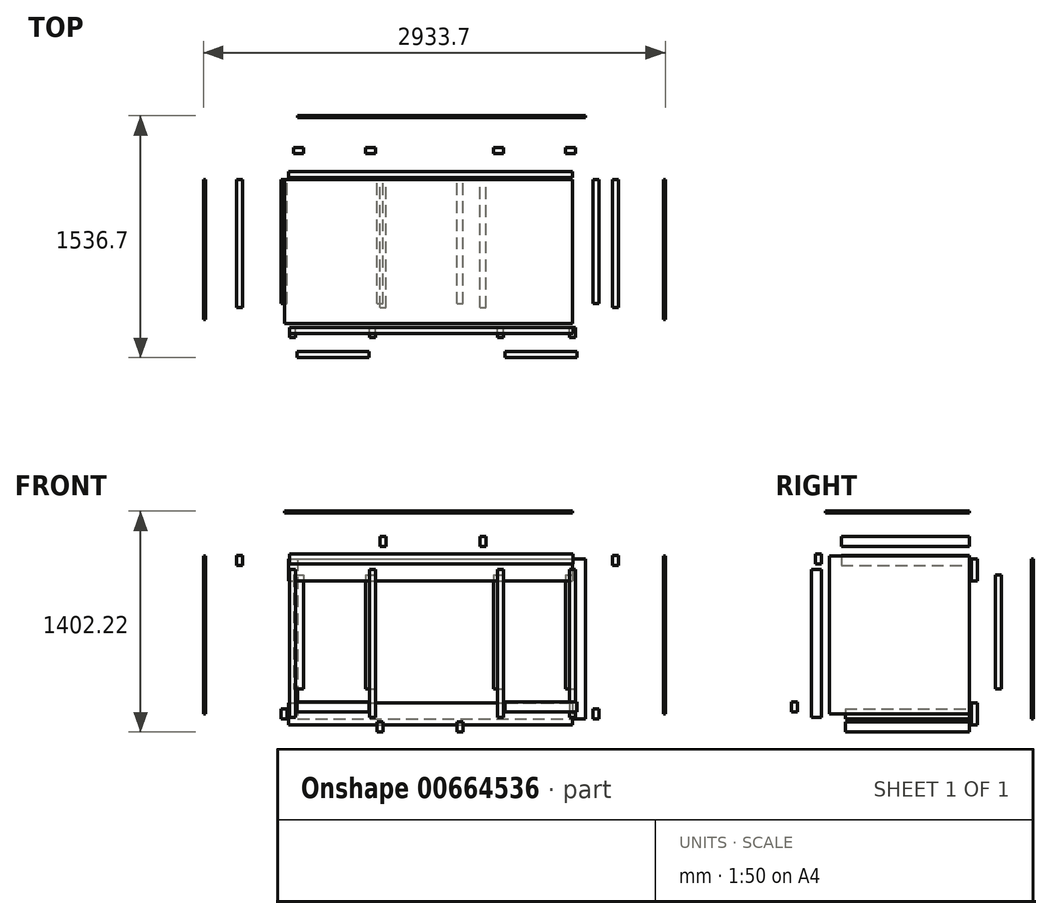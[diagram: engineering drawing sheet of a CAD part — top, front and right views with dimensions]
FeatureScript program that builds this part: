
annotation { "Feature Type Name" : "Feature", "Feature Type Description" : "" }
export const myFeature = defineFeature(function(context is Context, id is Id, definition is map)
    precondition{}
    {
        {
            var Q0;
            Q0=qCreatedBy(makeId("Front.planeOp"),FACE);
            var sketch = newSketch(context, id + "F0", { "sketchPlane" : qUnion([Q0])});
            skLineSegment(sketch, "E0.bottom", {"start": v(-77.6, 167.5) * mm, "end": v(1751.2, 167.5) * mm});
            skLineSegment(sketch, "E0.top", {"start": v(-77.6, 154.8) * mm, "end": v(1751.2, 154.8) * mm});
            skLineSegment(sketch, "E0.left", {"start": v(-77.6, 167.5) * mm, "end": v(-77.6, 154.8) * mm});
            skLineSegment(sketch, "E0.right", {"start": v(1751.2, 167.5) * mm, "end": v(1751.2, 154.8) * mm});
            skSolve(sketch);
        }
        {
            var Q0;
            Q0=qSketchRegion(id+"F0",true);
            extrude(context, id + "F1", {"entities" : qUnion([Q0]), "depth" : 914.4 * mm, "offsetDistance" : 25.4 * mm});
        }
        {
            var Q0;
            Q0=qCreatedBy(makeId("Front.planeOp"),FACE);
            var sketch = newSketch(context, id + "F2", { "sketchPlane" : qUnion([Q0])});
            skLineSegment(sketch, "E1.bottom", {"start": v(-96.67, 148.12) * mm, "end": v(1706.73, 148.12) * mm});
            skLineSegment(sketch, "E1.top", {"start": v(-96.67, 84.62) * mm, "end": v(1706.73, 84.62) * mm});
            skLineSegment(sketch, "E1.left", {"start": v(-96.67, 148.12) * mm, "end": v(-96.67, 84.62) * mm});
            skLineSegment(sketch, "E1.right", {"start": v(1706.73, 148.12) * mm, "end": v(1706.73, 84.62) * mm});
            skSolve(sketch);
        }
        {
            var Q0;
            Q0=qSketchRegion(id+"F2",true);
            extrude(context, id + "F3", {"entities" : qUnion([Q0]), "depth" : 38.1 * mm, "offsetDistance" : 25.4 * mm});
        }
        {
            var Q0;
            Q0=makeQuery(id+"F3.opExtrude","SWEPT_BODY",BODY,{"disambiguationData":[OSD([sQuery(id+"F2.wireOp",EDGE,"E1.bottom"),sQuery(id+"F2.wireOp",EDGE,"E1.top"),sQuery(id+"F2.wireOp",EDGE,"E1.left"),sQuery(id+"F2.wireOp",EDGE,"E1.right")])]});
            transform(context, id + "F4", {"entities" : qUnion([Q0]), "transformType" : TransformType.TRANSLATION_3D, "dx" : -762 * mm, "dy" : -939.8 * mm, "dz" : 0 * mm, "makeCopy" : false});
        }
        {
            var Q0;
            Q0=makeQuery(id+"F1.opExtrude","SWEPT_BODY",BODY,{"disambiguationData":[OSD([sQuery(id+"F0.wireOp",EDGE,"E0.bottom"),sQuery(id+"F0.wireOp",EDGE,"E0.top"),sQuery(id+"F0.wireOp",EDGE,"E0.left"),sQuery(id+"F0.wireOp",EDGE,"E0.right")])]});
            transform(context, id + "F5", {"entities" : qUnion([Q0]), "transformType" : TransformType.TRANSLATION_3D, "dx" : -812.8 * mm, "dy" : 0 * mm, "dz" : 0 * mm, "makeCopy" : false});
        }
        {
            var Q0;
            Q0=qCreatedBy(makeId("Front.planeOp"),FACE);
            var sketch = newSketch(context, id + "F6", { "sketchPlane" : qUnion([Q0])});
            skLineSegment(sketch, "E2.bottom", {"start": v(-857.8, 557.43) * mm, "end": v(-819.7, 557.43) * mm});
            skLineSegment(sketch, "E2.top", {"start": v(-857.8, -382.37) * mm, "end": v(-819.7, -382.37) * mm});
            skLineSegment(sketch, "E2.left", {"start": v(-857.8, 557.43) * mm, "end": v(-857.8, -382.37) * mm});
            skLineSegment(sketch, "E2.right", {"start": v(-819.7, 557.43) * mm, "end": v(-819.7, -382.37) * mm});
            skSolve(sketch);
        }
        {
            var Q0;
            Q0=qSketchRegion(id+"F6",true);
            extrude(context, id + "F7", {"entities" : qUnion([Q0]), "depth" : 63.5 * mm, "offsetDistance" : 25.4 * mm});
        }
        {
            var Q0;
            Q0=makeQuery(id+"F7.opExtrude","SWEPT_BODY",BODY,{"disambiguationData":[OSD([sQuery(id+"F6.wireOp",EDGE,"E2.bottom"),sQuery(id+"F6.wireOp",EDGE,"E2.top"),sQuery(id+"F6.wireOp",EDGE,"E2.left"),sQuery(id+"F6.wireOp",EDGE,"E2.right")])]});
            transform(context, id + "F8", {"entities" : qUnion([Q0]), "transformType" : TransformType.TRANSLATION_3D, "dx" : 0 * mm, "dy" : -939.8 * mm, "dz" : -508 * mm, "makeCopy" : false});
        }
        {
            var Q0;
            Q0=makeQuery(id+"F7.opExtrude","SWEPT_BODY",BODY,{"disambiguationData":[OSD([sQuery(id+"F6.wireOp",EDGE,"E2.bottom"),sQuery(id+"F6.wireOp",EDGE,"E2.top"),sQuery(id+"F6.wireOp",EDGE,"E2.left"),sQuery(id+"F6.wireOp",EDGE,"E2.right")])]});
            transform(context, id + "F9", {"entities" : qUnion([Q0]), "transformType" : TransformType.TRANSLATION_3D, "dx" : 1778 * mm, "dy" : 0 * mm, "dz" : 0 * mm, "makeCopy" : true});
        }
        {
            var Q0;
            Q0=makeQuery(id+"F7.opExtrude","SWEPT_BODY",BODY,{"disambiguationData":[OSD([sQuery(id+"F6.wireOp",EDGE,"E2.bottom"),sQuery(id+"F6.wireOp",EDGE,"E2.top"),sQuery(id+"F6.wireOp",EDGE,"E2.left"),sQuery(id+"F6.wireOp",EDGE,"E2.right")])]});
            transform(context, id + "F10", {"entities" : qUnion([Q0]), "transformType" : TransformType.TRANSLATION_3D, "dx" : 508 * mm, "dy" : 0 * mm, "dz" : 0 * mm, "makeCopy" : true});
        }
        {
            var Q0;
            Q0=makeQuery(id+"F7.opExtrude","SWEPT_BODY",BODY,{"disambiguationData":[OSD([sQuery(id+"F6.wireOp",EDGE,"E2.bottom"),sQuery(id+"F6.wireOp",EDGE,"E2.top"),sQuery(id+"F6.wireOp",EDGE,"E2.left"),sQuery(id+"F6.wireOp",EDGE,"E2.right")])]});
            transform(context, id + "F11", {"entities" : qUnion([Q0]), "transformType" : TransformType.TRANSLATION_3D, "dx" : 1320.8 * mm, "dy" : 0 * mm, "dz" : 0 * mm, "makeCopy" : true});
        }
        {
            var Q0;
            Q0=qCreatedBy(makeId("Front.planeOp"),FACE);
            var sketch = newSketch(context, id + "F12", { "sketchPlane" : qUnion([Q0])});
            skLineSegment(sketch, "E3.bottom", {"start": v(-940.02, 138.97) * mm, "end": v(-901.92, 138.97) * mm});
            skLineSegment(sketch, "E3.top", {"start": v(-940.02, 75.47) * mm, "end": v(-901.92, 75.47) * mm});
            skLineSegment(sketch, "E3.left", {"start": v(-940.02, 138.97) * mm, "end": v(-940.02, 75.47) * mm});
            skLineSegment(sketch, "E3.right", {"start": v(-901.92, 138.97) * mm, "end": v(-901.92, 75.47) * mm});
            skSolve(sketch);
        }
        {
            var Q0;
            Q0=qSketchRegion(id+"F12",true);
            extrude(context, id + "F13", {"entities" : qUnion([Q0]), "depth" : 812.8 * mm, "offsetDistance" : 25.4 * mm});
        }
        {
            var Q0;
            Q0=makeQuery(id+"F13.opExtrude","SWEPT_BODY",BODY,{"disambiguationData":[OSD([sQuery(id+"F12.wireOp",EDGE,"E3.bottom"),sQuery(id+"F12.wireOp",EDGE,"E3.top"),sQuery(id+"F12.wireOp",EDGE,"E3.left"),sQuery(id+"F12.wireOp",EDGE,"E3.right")])]});
            transform(context, id + "F14", {"entities" : qUnion([Q0]), "transformType" : TransformType.TRANSLATION_3D, "dx" : 1879.6 * mm, "dy" : 0 * mm, "dz" : 0 * mm, "makeCopy" : true});
        }
        {
            var Q0;
            Q0=qCreatedBy(makeId("Front.planeOp"),FACE);
            var sketch = newSketch(context, id + "F15", { "sketchPlane" : qUnion([Q0])});
            skLineSegment(sketch, "E4.bottom", {"start": v(-862.45, 42) * mm, "end": v(940.95, 42) * mm});
            skLineSegment(sketch, "E4.top", {"start": v(-862.45, -97.7) * mm, "end": v(940.95, -97.7) * mm});
            skLineSegment(sketch, "E4.left", {"start": v(-862.45, 42) * mm, "end": v(-862.45, -97.7) * mm});
            skLineSegment(sketch, "E4.right", {"start": v(940.95, 42) * mm, "end": v(940.95, -97.7) * mm});
            skSolve(sketch);
        }
        {
            var Q0;
            Q0=qSketchRegion(id+"F15",true);
            extrude(context, id + "F16", {"entities" : qUnion([Q0]), "depth" : 38.1 * mm, "offsetDistance" : 25.4 * mm});
        }
        {
            var Q0;
            Q0=makeQuery(id+"F16.opExtrude","SWEPT_BODY",BODY,{"disambiguationData":[OSD([sQuery(id+"F15.wireOp",EDGE,"E4.bottom"),sQuery(id+"F15.wireOp",EDGE,"E4.top"),sQuery(id+"F15.wireOp",EDGE,"E4.left"),sQuery(id+"F15.wireOp",EDGE,"E4.right")])]});
            transform(context, id + "F17", {"entities" : qUnion([Q0]), "transformType" : TransformType.TRANSLATION_3D, "dx" : 0 * mm, "dy" : 0 * mm, "dz" : -762 * mm, "makeCopy" : true});
        }
        {
            var Q0;
            Q0=makeQuery(id+"F13.opExtrude","SWEPT_BODY",BODY,{"disambiguationData":[OSD([sQuery(id+"F12.wireOp",EDGE,"E3.bottom"),sQuery(id+"F12.wireOp",EDGE,"E3.top"),sQuery(id+"F12.wireOp",EDGE,"E3.left"),sQuery(id+"F12.wireOp",EDGE,"E3.right")])]});
            transform(context, id + "F18", {"entities" : qUnion([Q0]), "transformType" : TransformType.TRANSLATION_3D, "dx" : 0 * mm, "dy" : 0 * mm, "dz" : -939.8 * mm, "makeCopy" : true});
        }
        {
            var Q0;
            Q0=makeQuery(id+"F14.opPattern","COPY",BODY,{"derivedFrom":makeQuery(id+"F13.opExtrude","SWEPT_BODY",BODY,{"disambiguationData":[OSD([sQuery(id+"F12.wireOp",EDGE,"E3.bottom"),sQuery(id+"F12.wireOp",EDGE,"E3.top"),sQuery(id+"F12.wireOp",EDGE,"E3.left"),sQuery(id+"F12.wireOp",EDGE,"E3.right")])]}),"instanceName":"1"});
            transform(context, id + "F19", {"entities" : qUnion([Q0]), "transformType" : TransformType.TRANSLATION_3D, "dx" : 0 * mm, "dy" : 0 * mm, "dz" : -939.8 * mm, "makeCopy" : true});
        }
        {
            var Q0;
            Q0=qCreatedBy(makeId("Front.planeOp"),FACE);
            var sketch = newSketch(context, id + "F20", { "sketchPlane" : qUnion([Q0])});
            skLineSegment(sketch, "E5.bottom", {"start": v(-809.8, -791.75) * mm, "end": v(-352.6, -791.75) * mm});
            skLineSegment(sketch, "E5.top", {"start": v(-809.8, -855.25) * mm, "end": v(-352.6, -855.25) * mm});
            skLineSegment(sketch, "E5.left", {"start": v(-809.8, -791.75) * mm, "end": v(-809.8, -855.25) * mm});
            skLineSegment(sketch, "E5.right", {"start": v(-352.6, -791.75) * mm, "end": v(-352.6, -855.25) * mm});
            skSolve(sketch);
        }
        {
            var Q0;
            Q0=qSketchRegion(id+"F20",true);
            extrude(context, id + "F21", {"entities" : qUnion([Q0]), "depth" : 38.1 * mm, "offsetDistance" : 25.4 * mm});
        }
        {
            var Q0;
            Q0=makeQuery(id+"F21.opExtrude","SWEPT_BODY",BODY,{"disambiguationData":[OSD([sQuery(id+"F20.wireOp",EDGE,"E5.bottom"),sQuery(id+"F20.wireOp",EDGE,"E5.top"),sQuery(id+"F20.wireOp",EDGE,"E5.left"),sQuery(id+"F20.wireOp",EDGE,"E5.right")])]});
            transform(context, id + "F22", {"entities" : qUnion([Q0]), "transformType" : TransformType.TRANSLATION_3D, "dx" : 0 * mm, "dy" : -965.2 * mm, "dz" : 0 * mm, "makeCopy" : false});
        }
        {
            var Q0;
            Q0=makeQuery(id+"F21.opExtrude","SWEPT_BODY",BODY,{"disambiguationData":[OSD([sQuery(id+"F20.wireOp",EDGE,"E5.bottom"),sQuery(id+"F20.wireOp",EDGE,"E5.top"),sQuery(id+"F20.wireOp",EDGE,"E5.left"),sQuery(id+"F20.wireOp",EDGE,"E5.right")])]});
            transform(context, id + "F23", {"entities" : qUnion([Q0]), "transformType" : TransformType.TRANSLATION_3D, "dx" : 1320.8 * mm, "dy" : 0 * mm, "dz" : 0 * mm, "makeCopy" : true});
        }
        {
            var Q0;
            Q0=makeQuery(id+"F13.opExtrude","SWEPT_BODY",BODY,{"disambiguationData":[OSD([sQuery(id+"F12.wireOp",EDGE,"E3.bottom"),sQuery(id+"F12.wireOp",EDGE,"E3.top"),sQuery(id+"F12.wireOp",EDGE,"E3.left"),sQuery(id+"F12.wireOp",EDGE,"E3.right")])]});
            transform(context, id + "F24", {"entities" : qUnion([Q0]), "transformType" : TransformType.TRANSLATION_3D, "dx" : 508 * mm, "dy" : 0 * mm, "dz" : 0 * mm, "makeCopy" : true});
        }
        {
            var Q0;
            Q0=makeQuery(id+"F13.opExtrude","SWEPT_BODY",BODY,{"disambiguationData":[OSD([sQuery(id+"F12.wireOp",EDGE,"E3.bottom"),sQuery(id+"F12.wireOp",EDGE,"E3.top"),sQuery(id+"F12.wireOp",EDGE,"E3.left"),sQuery(id+"F12.wireOp",EDGE,"E3.right")])]});
            transform(context, id + "F25", {"entities" : qUnion([Q0]), "transformType" : TransformType.TRANSLATION_3D, "dx" : 1320.8 * mm, "dy" : 0 * mm, "dz" : 0 * mm, "makeCopy" : true});
        }
        {
            var Q0;
            Q0=qCreatedBy(makeId("Front.planeOp"),FACE);
            var sketch = newSketch(context, id + "F26", { "sketchPlane" : qUnion([Q0])});
            skLineSegment(sketch, "E6.bottom", {"start": v(-831.16, 15.51) * mm, "end": v(-767.66, 15.51) * mm});
            skLineSegment(sketch, "E6.top", {"start": v(-831.16, -708.39) * mm, "end": v(-767.66, -708.39) * mm});
            skLineSegment(sketch, "E6.left", {"start": v(-831.16, 15.51) * mm, "end": v(-831.16, -708.39) * mm});
            skLineSegment(sketch, "E6.right", {"start": v(-767.66, 15.51) * mm, "end": v(-767.66, -708.39) * mm});
            skSolve(sketch);
        }
        {
            var Q0;
            Q0=qSketchRegion(id+"F26",true);
            extrude(context, id + "F27", {"entities" : qUnion([Q0]), "depth" : 38.1 * mm, "offsetDistance" : 25.4 * mm});
        }
        {
            var Q0;
            Q0=makeQuery(id+"F27.opExtrude","SWEPT_BODY",BODY,{"disambiguationData":[OSD([sQuery(id+"F26.wireOp",EDGE,"E6.bottom"),sQuery(id+"F26.wireOp",EDGE,"E6.top"),sQuery(id+"F26.wireOp",EDGE,"E6.left"),sQuery(id+"F26.wireOp",EDGE,"E6.right")])]});
            transform(context, id + "F28", {"entities" : qUnion([Q0]), "transformType" : TransformType.TRANSLATION_3D, "dx" : 0 * mm, "dy" : 76.2 * mm, "dz" : 0 * mm, "makeCopy" : false});
        }
        {
            var Q0;
            Q0=makeQuery(id+"F27.opExtrude","SWEPT_BODY",BODY,{"disambiguationData":[OSD([sQuery(id+"F26.wireOp",EDGE,"E6.bottom"),sQuery(id+"F26.wireOp",EDGE,"E6.top"),sQuery(id+"F26.wireOp",EDGE,"E6.left"),sQuery(id+"F26.wireOp",EDGE,"E6.right")])]});
            transform(context, id + "F29", {"entities" : qUnion([Q0]), "transformType" : TransformType.TRANSLATION_3D, "dx" : 457.2 * mm, "dy" : 0 * mm, "dz" : 0 * mm, "makeCopy" : true});
        }
        {
            var Q0;
            Q0=makeQuery(id+"F27.opExtrude","SWEPT_BODY",BODY,{"disambiguationData":[OSD([sQuery(id+"F26.wireOp",EDGE,"E6.bottom"),sQuery(id+"F26.wireOp",EDGE,"E6.top"),sQuery(id+"F26.wireOp",EDGE,"E6.left"),sQuery(id+"F26.wireOp",EDGE,"E6.right")])]});
            transform(context, id + "F30", {"entities" : qUnion([Q0]), "transformType" : TransformType.TRANSLATION_3D, "dx" : 1270 * mm, "dy" : 0 * mm, "dz" : 0 * mm, "makeCopy" : true});
        }
        {
            var Q0;
            Q0=makeQuery(id+"F27.opExtrude","SWEPT_BODY",BODY,{"disambiguationData":[OSD([sQuery(id+"F26.wireOp",EDGE,"E6.bottom"),sQuery(id+"F26.wireOp",EDGE,"E6.top"),sQuery(id+"F26.wireOp",EDGE,"E6.left"),sQuery(id+"F26.wireOp",EDGE,"E6.right")])]});
            transform(context, id + "F31", {"entities" : qUnion([Q0]), "transformType" : TransformType.TRANSLATION_3D, "dx" : 1727.2 * mm, "dy" : 0 * mm, "dz" : 0 * mm, "makeCopy" : true});
        }
        {
            var Q0;
            Q0=qCreatedBy(makeId("Front.planeOp"),FACE);
            var sketch = newSketch(context, id + "F32", { "sketchPlane" : qUnion([Q0])});
            skLineSegment(sketch, "E7.bottom", {"start": v(-1023.09, 135.28) * mm, "end": v(-1010.39, 135.28) * mm});
            skLineSegment(sketch, "E7.top", {"start": v(-1023.09, -868.02) * mm, "end": v(-1010.39, -868.02) * mm});
            skLineSegment(sketch, "E7.left", {"start": v(-1023.09, 135.28) * mm, "end": v(-1023.09, -868.02) * mm});
            skLineSegment(sketch, "E7.right", {"start": v(-1010.39, 135.28) * mm, "end": v(-1010.39, -868.02) * mm});
            skSolve(sketch);
        }
        {
            var Q0;
            Q0=qSketchRegion(id+"F32",true);
            extrude(context, id + "F33", {"entities" : qUnion([Q0]), "depth" : 889 * mm, "offsetDistance" : 25.4 * mm});
        }
        {
            var Q0;
            Q0=makeQuery(id+"F33.opExtrude","SWEPT_BODY",BODY,{"disambiguationData":[OSD([sQuery(id+"F32.wireOp",EDGE,"E7.bottom"),sQuery(id+"F32.wireOp",EDGE,"E7.top"),sQuery(id+"F32.wireOp",EDGE,"E7.left"),sQuery(id+"F32.wireOp",EDGE,"E7.right")])]});
            transform(context, id + "F34", {"entities" : qUnion([Q0]), "transformType" : TransformType.TRANSLATION_3D, "dx" : 2032 * mm, "dy" : 0 * mm, "dz" : 0 * mm, "makeCopy" : true});
        }
        {
            var Q0;
            Q0=qCreatedBy(makeId("Front.planeOp"),FACE);
            var sketch = newSketch(context, id + "F35", { "sketchPlane" : qUnion([Q0])});
            skLineSegment(sketch, "E8.bottom", {"start": v(-806.57, 117.24) * mm, "end": v(1022.23, 117.24) * mm});
            skLineSegment(sketch, "E8.top", {"start": v(-806.57, -898.76) * mm, "end": v(1022.23, -898.76) * mm});
            skLineSegment(sketch, "E8.left", {"start": v(-806.57, 117.24) * mm, "end": v(-806.57, -898.76) * mm});
            skLineSegment(sketch, "E8.right", {"start": v(1022.23, 117.24) * mm, "end": v(1022.23, -898.76) * mm});
            skSolve(sketch);
        }
        {
            var Q0;
            Q0=qSketchRegion(id+"F35",true);
            extrude(context, id + "F36", {"entities" : qUnion([Q0]), "depth" : 12.7 * mm, "offsetDistance" : 25.4 * mm});
        }
        {
            var Q0;
            Q0=makeQuery(id+"F36.opExtrude","SWEPT_BODY",BODY,{"disambiguationData":[OSD([sQuery(id+"F35.wireOp",EDGE,"E8.bottom"),sQuery(id+"F35.wireOp",EDGE,"E8.top"),sQuery(id+"F35.wireOp",EDGE,"E8.left"),sQuery(id+"F35.wireOp",EDGE,"E8.right")])]});
            transform(context, id + "F37", {"entities" : qUnion([Q0]), "transformType" : TransformType.TRANSLATION_3D, "dx" : 0 * mm, "dy" : 152.4 * mm, "dz" : 0 * mm, "makeCopy" : false});
        }
        {
            var Q0;
            Q0=qCreatedBy(makeId("Front.planeOp"),FACE);
            var sketch = newSketch(context, id + "F38", { "sketchPlane" : qUnion([Q0])});
            skLineSegment(sketch, "E9.bottom", {"start": v(-300.73, -790.22) * mm, "end": v(-262.63, -790.22) * mm});
            skLineSegment(sketch, "E9.top", {"start": v(-300.73, -853.72) * mm, "end": v(-262.63, -853.72) * mm});
            skLineSegment(sketch, "E9.left", {"start": v(-300.73, -790.22) * mm, "end": v(-300.73, -853.72) * mm});
            skLineSegment(sketch, "E9.right", {"start": v(-262.63, -790.22) * mm, "end": v(-262.63, -853.72) * mm});
            skSolve(sketch);
        }
        {
            var Q0;
            Q0=qSketchRegion(id+"F38",true);
            extrude(context, id + "F39", {"entities" : qUnion([Q0]), "depth" : 787.4 * mm, "offsetDistance" : 25.4 * mm});
        }
        {
            var Q0;
            Q0=makeQuery(id+"F39.opExtrude","SWEPT_BODY",BODY,{"disambiguationData":[OSD([sQuery(id+"F38.wireOp",EDGE,"E9.bottom"),sQuery(id+"F38.wireOp",EDGE,"E9.top"),sQuery(id+"F38.wireOp",EDGE,"E9.left"),sQuery(id+"F38.wireOp",EDGE,"E9.right")])]});
            transform(context, id + "F40", {"entities" : qUnion([Q0]), "transformType" : TransformType.TRANSLATION_3D, "dx" : 508 * mm, "dy" : 0 * mm, "dz" : 0 * mm, "makeCopy" : true});
        }
        {
            var Q0;
            Q0=makeQuery(id+"F19.opPattern","COPY",BODY,{"derivedFrom":makeQuery(id+"F14.opPattern","COPY",BODY,{"derivedFrom":makeQuery(id+"F13.opExtrude","SWEPT_BODY",BODY,{"disambiguationData":[OSD([sQuery(id+"F12.wireOp",EDGE,"E3.bottom"),sQuery(id+"F12.wireOp",EDGE,"E3.top"),sQuery(id+"F12.wireOp",EDGE,"E3.left"),sQuery(id+"F12.wireOp",EDGE,"E3.right")])]}),"instanceName":"1"}),"instanceName":"1"});
            deleteBodies(context, id + "F41", {"entities" : qUnion([Q0])});
        }
        {
            var Q0;
            Q0=makeQuery(id+"F18.opPattern","COPY",BODY,{"derivedFrom":makeQuery(id+"F13.opExtrude","SWEPT_BODY",BODY,{"disambiguationData":[OSD([sQuery(id+"F12.wireOp",EDGE,"E3.bottom"),sQuery(id+"F12.wireOp",EDGE,"E3.top"),sQuery(id+"F12.wireOp",EDGE,"E3.left"),sQuery(id+"F12.wireOp",EDGE,"E3.right")])]}),"instanceName":"1"});
            deleteBodies(context, id + "F42", {"entities" : qUnion([Q0])});
        }
        {
            var Q0;
            Q0=makeQuery(id+"F24.opPattern","COPY",BODY,{"derivedFrom":makeQuery(id+"F13.opExtrude","SWEPT_BODY",BODY,{"disambiguationData":[OSD([sQuery(id+"F12.wireOp",EDGE,"E3.bottom"),sQuery(id+"F12.wireOp",EDGE,"E3.top"),sQuery(id+"F12.wireOp",EDGE,"E3.left"),sQuery(id+"F12.wireOp",EDGE,"E3.right")])]}),"instanceName":"1"});
            deleteBodies(context, id + "F43", {"entities" : qUnion([Q0])});
        }
        {
            var Q0;
            Q0=makeQuery(id+"F25.opPattern","COPY",BODY,{"derivedFrom":makeQuery(id+"F13.opExtrude","SWEPT_BODY",BODY,{"disambiguationData":[OSD([sQuery(id+"F12.wireOp",EDGE,"E3.bottom"),sQuery(id+"F12.wireOp",EDGE,"E3.top"),sQuery(id+"F12.wireOp",EDGE,"E3.left"),sQuery(id+"F12.wireOp",EDGE,"E3.right")])]}),"instanceName":"1"});
            deleteBodies(context, id + "F44", {"entities" : qUnion([Q0])});
        }
        {
            var Q0;
            Q0=qCreatedBy(makeId("Front.planeOp"),FACE);
            var sketch = newSketch(context, id + "F45", { "sketchPlane" : qUnion([Q0])});
            skLineSegment(sketch, "E10.bottom", {"start": v(-911.41, -835.62) * mm, "end": v(-873.31, -835.62) * mm});
            skLineSegment(sketch, "E10.top", {"start": v(-911.41, -899.12) * mm, "end": v(-873.31, -899.12) * mm});
            skLineSegment(sketch, "E10.left", {"start": v(-911.41, -835.62) * mm, "end": v(-911.41, -899.12) * mm});
            skLineSegment(sketch, "E10.right", {"start": v(-873.31, -835.62) * mm, "end": v(-873.31, -899.12) * mm});
            skSolve(sketch);
        }
        {
            var Q0;
            Q0=qSketchRegion(id+"F45",true);
            extrude(context, id + "F46", {"entities" : qUnion([Q0]), "depth" : 787.4 * mm, "offsetDistance" : 25.4 * mm});
        }
        {
            var Q0;
            Q0=makeQuery(id+"F46.opExtrude","SWEPT_BODY",BODY,{"disambiguationData":[OSD([sQuery(id+"F45.wireOp",EDGE,"E10.bottom"),sQuery(id+"F45.wireOp",EDGE,"E10.top"),sQuery(id+"F45.wireOp",EDGE,"E10.left"),sQuery(id+"F45.wireOp",EDGE,"E10.right")])]});
            transform(context, id + "F47", {"entities" : qUnion([Q0]), "transformType" : TransformType.TRANSLATION_3D, "dx" : 1981.2 * mm, "dy" : 0 * mm, "dz" : 0 * mm, "makeCopy" : true});
        }
        {
            var Q0;
            Q0=makeQuery(id+"F46.opExtrude","SWEPT_BODY",BODY,{"disambiguationData":[OSD([sQuery(id+"F45.wireOp",EDGE,"E10.bottom"),sQuery(id+"F45.wireOp",EDGE,"E10.top"),sQuery(id+"F45.wireOp",EDGE,"E10.left"),sQuery(id+"F45.wireOp",EDGE,"E10.right")])]});
            transform(context, id + "F48", {"entities" : qUnion([Q0]), "transformType" : TransformType.TRANSLATION_3D, "dx" : 533.4 * mm, "dy" : 0 * mm, "dz" : 762 * mm, "makeCopy" : true});
        }
        {
            var Q0;
            Q0=makeQuery(id+"F48.opPattern","COPY",BODY,{"derivedFrom":makeQuery(id+"F46.opExtrude","SWEPT_BODY",BODY,{"disambiguationData":[OSD([sQuery(id+"F45.wireOp",EDGE,"E10.bottom"),sQuery(id+"F45.wireOp",EDGE,"E10.top"),sQuery(id+"F45.wireOp",EDGE,"E10.left"),sQuery(id+"F45.wireOp",EDGE,"E10.right")])]}),"instanceName":"1"});
            transform(context, id + "F49", {"entities" : qUnion([Q0]), "transformType" : TransformType.TRANSLATION_3D, "dx" : 635 * mm, "dy" : 0 * mm, "dz" : 0 * mm, "makeCopy" : true});
        }
        {
            var Q0;
            Q0=makeQuery(id+"F48.opPattern","COPY",BODY,{"derivedFrom":makeQuery(id+"F46.opExtrude","SWEPT_BODY",BODY,{"disambiguationData":[OSD([sQuery(id+"F45.wireOp",EDGE,"E10.bottom"),sQuery(id+"F45.wireOp",EDGE,"E10.top"),sQuery(id+"F45.wireOp",EDGE,"E10.left"),sQuery(id+"F45.wireOp",EDGE,"E10.right")])]}),"instanceName":"1"});
            deleteBodies(context, id + "F50", {"entities" : qUnion([Q0])});
        }
        {
            var Q0;
            Q0=makeQuery(id+"F49.opPattern","COPY",BODY,{"derivedFrom":makeQuery(id+"F48.opPattern","COPY",BODY,{"derivedFrom":makeQuery(id+"F46.opExtrude","SWEPT_BODY",BODY,{"disambiguationData":[OSD([sQuery(id+"F45.wireOp",EDGE,"E10.bottom"),sQuery(id+"F45.wireOp",EDGE,"E10.top"),sQuery(id+"F45.wireOp",EDGE,"E10.left"),sQuery(id+"F45.wireOp",EDGE,"E10.right")])]}),"instanceName":"1"}),"instanceName":"1"});
            deleteBodies(context, id + "F51", {"entities" : qUnion([Q0])});
        }
        {
            var Q0;
            Q0=qCreatedBy(makeId("Front.planeOp"),FACE);
            var sketch = newSketch(context, id + "F52", { "sketchPlane" : qUnion([Q0])});
            skLineSegment(sketch, "E11.bottom", {"start": v(-283.08, 7.53) * mm, "end": v(-244.98, 7.53) * mm});
            skLineSegment(sketch, "E11.top", {"start": v(-283.08, -55.97) * mm, "end": v(-244.98, -55.97) * mm});
            skLineSegment(sketch, "E11.left", {"start": v(-283.08, 7.53) * mm, "end": v(-283.08, -55.97) * mm});
            skLineSegment(sketch, "E11.right", {"start": v(-244.98, 7.53) * mm, "end": v(-244.98, -55.97) * mm});
            skSolve(sketch);
        }
        {
            var Q0;
            Q0=qSketchRegion(id+"F52",true);
            extrude(context, id + "F53", {"entities" : qUnion([Q0]), "depth" : 812.8 * mm, "offsetDistance" : 25.4 * mm});
        }
        {
            var Q0;
            Q0=makeQuery(id+"F53.opExtrude","SWEPT_BODY",BODY,{"disambiguationData":[OSD([sQuery(id+"F52.wireOp",EDGE,"E11.bottom"),sQuery(id+"F52.wireOp",EDGE,"E11.top"),sQuery(id+"F52.wireOp",EDGE,"E11.left"),sQuery(id+"F52.wireOp",EDGE,"E11.right")])]});
            transform(context, id + "F54", {"entities" : qUnion([Q0]), "transformType" : TransformType.TRANSLATION_3D, "dx" : 635 * mm, "dy" : 0 * mm, "dz" : 0 * mm, "makeCopy" : true});
        }
        {
            var Q0;
            Q0=makeQuery(id+"F33.opExtrude","SWEPT_BODY",BODY,{"disambiguationData":[OSD([sQuery(id+"F32.wireOp",EDGE,"E7.bottom"),sQuery(id+"F32.wireOp",EDGE,"E7.top"),sQuery(id+"F32.wireOp",EDGE,"E7.left"),sQuery(id+"F32.wireOp",EDGE,"E7.right")])]});
            transform(context, id + "F55", {"entities" : qUnion([Q0]), "transformType" : TransformType.TRANSLATION_3D, "dx" : -381 * mm, "dy" : 0 * mm, "dz" : 0 * mm, "makeCopy" : false});
        }
        {
            var Q0;
            Q0=makeQuery(id+"F34.opPattern","COPY",BODY,{"derivedFrom":makeQuery(id+"F33.opExtrude","SWEPT_BODY",BODY,{"disambiguationData":[OSD([sQuery(id+"F32.wireOp",EDGE,"E7.bottom"),sQuery(id+"F32.wireOp",EDGE,"E7.top"),sQuery(id+"F32.wireOp",EDGE,"E7.left"),sQuery(id+"F32.wireOp",EDGE,"E7.right")])]}),"instanceName":"1"});
            transform(context, id + "F56", {"entities" : qUnion([Q0]), "transformType" : TransformType.TRANSLATION_3D, "dx" : -2286 * mm, "dy" : 0 * mm, "dz" : 0 * mm, "makeCopy" : false});
        }
        {
            var Q0;
            Q0=makeQuery(id+"F34.opPattern","COPY",BODY,{"derivedFrom":makeQuery(id+"F33.opExtrude","SWEPT_BODY",BODY,{"disambiguationData":[OSD([sQuery(id+"F32.wireOp",EDGE,"E7.bottom"),sQuery(id+"F32.wireOp",EDGE,"E7.top"),sQuery(id+"F32.wireOp",EDGE,"E7.left"),sQuery(id+"F32.wireOp",EDGE,"E7.right")])]}),"instanceName":"1"});
            transform(context, id + "F57", {"entities" : qUnion([Q0]), "transformType" : TransformType.TRANSLATION_3D, "dx" : 2794 * mm, "dy" : 0 * mm, "dz" : 0 * mm, "makeCopy" : false});
        }
        {
            var Q0;
            Q0=makeQuery(id+"F1.opExtrude","SWEPT_BODY",BODY,{"disambiguationData":[OSD([sQuery(id+"F0.wireOp",EDGE,"E0.bottom"),sQuery(id+"F0.wireOp",EDGE,"E0.top"),sQuery(id+"F0.wireOp",EDGE,"E0.left"),sQuery(id+"F0.wireOp",EDGE,"E0.right")])]});
            transform(context, id + "F58", {"entities" : qUnion([Q0]), "transformType" : TransformType.TRANSLATION_3D, "dx" : 0 * mm, "dy" : 0 * mm, "dz" : 254 * mm, "makeCopy" : false});
        }
        {
            var Q0;
            Q0=makeQuery(id+"F36.opExtrude","SWEPT_BODY",BODY,{"disambiguationData":[OSD([sQuery(id+"F35.wireOp",EDGE,"E8.bottom"),sQuery(id+"F35.wireOp",EDGE,"E8.top"),sQuery(id+"F35.wireOp",EDGE,"E8.left"),sQuery(id+"F35.wireOp",EDGE,"E8.right")])]});
            transform(context, id + "F59", {"entities" : qUnion([Q0]), "transformType" : TransformType.TRANSLATION_3D, "dx" : 0 * mm, "dy" : 254 * mm, "dz" : 0 * mm, "makeCopy" : false});
        }
        {
            var Q0;
            Q0=makeQuery(id+"F13.opExtrude","SWEPT_BODY",BODY,{"disambiguationData":[OSD([sQuery(id+"F12.wireOp",EDGE,"E3.bottom"),sQuery(id+"F12.wireOp",EDGE,"E3.top"),sQuery(id+"F12.wireOp",EDGE,"E3.left"),sQuery(id+"F12.wireOp",EDGE,"E3.right")])]});
            transform(context, id + "F60", {"entities" : qUnion([Q0]), "transformType" : TransformType.TRANSLATION_3D, "dx" : -254 * mm, "dy" : 0 * mm, "dz" : 0 * mm, "makeCopy" : false});
        }
        {
            var Q0;
            Q0=makeQuery(id+"F14.opPattern","COPY",BODY,{"derivedFrom":makeQuery(id+"F13.opExtrude","SWEPT_BODY",BODY,{"disambiguationData":[OSD([sQuery(id+"F12.wireOp",EDGE,"E3.bottom"),sQuery(id+"F12.wireOp",EDGE,"E3.top"),sQuery(id+"F12.wireOp",EDGE,"E3.left"),sQuery(id+"F12.wireOp",EDGE,"E3.right")])]}),"instanceName":"1"});
            transform(context, id + "F61", {"entities" : qUnion([Q0]), "transformType" : TransformType.TRANSLATION_3D, "dx" : 254 * mm, "dy" : 0 * mm, "dz" : 0 * mm, "makeCopy" : false});
        }
        {
            var Q0;
            Q0=makeQuery(id+"F53.opExtrude","SWEPT_BODY",BODY,{"disambiguationData":[OSD([sQuery(id+"F52.wireOp",EDGE,"E11.bottom"),sQuery(id+"F52.wireOp",EDGE,"E11.top"),sQuery(id+"F52.wireOp",EDGE,"E11.left"),sQuery(id+"F52.wireOp",EDGE,"E11.right")])]});
            transform(context, id + "F62", {"entities" : qUnion([Q0]), "transformType" : TransformType.TRANSLATION_3D, "dx" : 0 * mm, "dy" : 0 * mm, "dz" : 254 * mm, "makeCopy" : false});
        }
        {
            var Q0;
            Q0=makeQuery(id+"F54.opPattern","COPY",BODY,{"derivedFrom":makeQuery(id+"F53.opExtrude","SWEPT_BODY",BODY,{"disambiguationData":[OSD([sQuery(id+"F52.wireOp",EDGE,"E11.bottom"),sQuery(id+"F52.wireOp",EDGE,"E11.top"),sQuery(id+"F52.wireOp",EDGE,"E11.left"),sQuery(id+"F52.wireOp",EDGE,"E11.right")])]}),"instanceName":"1"});
            transform(context, id + "F63", {"entities" : qUnion([Q0]), "transformType" : TransformType.TRANSLATION_3D, "dx" : 0 * mm, "dy" : 0 * mm, "dz" : 254 * mm, "makeCopy" : false});
        }
        {
            var Q0;
            Q0=makeQuery(id+"F27.opExtrude","SWEPT_BODY",BODY,{"disambiguationData":[OSD([sQuery(id+"F26.wireOp",EDGE,"E6.bottom"),sQuery(id+"F26.wireOp",EDGE,"E6.top"),sQuery(id+"F26.wireOp",EDGE,"E6.left"),sQuery(id+"F26.wireOp",EDGE,"E6.right")])]});
            var Q1;
            Q1=makeQuery(id+"F29.opPattern","COPY",BODY,{"derivedFrom":makeQuery(id+"F27.opExtrude","SWEPT_BODY",BODY,{"disambiguationData":[OSD([sQuery(id+"F26.wireOp",EDGE,"E6.bottom"),sQuery(id+"F26.wireOp",EDGE,"E6.top"),sQuery(id+"F26.wireOp",EDGE,"E6.left"),sQuery(id+"F26.wireOp",EDGE,"E6.right")])]}),"instanceName":"1"});
            var Q2;
            Q2=makeQuery(id+"F30.opPattern","COPY",BODY,{"derivedFrom":makeQuery(id+"F27.opExtrude","SWEPT_BODY",BODY,{"disambiguationData":[OSD([sQuery(id+"F26.wireOp",EDGE,"E6.bottom"),sQuery(id+"F26.wireOp",EDGE,"E6.top"),sQuery(id+"F26.wireOp",EDGE,"E6.left"),sQuery(id+"F26.wireOp",EDGE,"E6.right")])]}),"instanceName":"1"});
            var Q3;
            Q3=makeQuery(id+"F31.opPattern","COPY",BODY,{"derivedFrom":makeQuery(id+"F27.opExtrude","SWEPT_BODY",BODY,{"disambiguationData":[OSD([sQuery(id+"F26.wireOp",EDGE,"E6.bottom"),sQuery(id+"F26.wireOp",EDGE,"E6.top"),sQuery(id+"F26.wireOp",EDGE,"E6.left"),sQuery(id+"F26.wireOp",EDGE,"E6.right")])]}),"instanceName":"1"});
            transform(context, id + "F64", {"entities" : qUnion([Q0, Q1, Q2, Q3]), "transformType" : TransformType.TRANSLATION_3D, "dx" : 0 * mm, "dy" : 127 * mm, "dz" : 0 * mm, "makeCopy" : false});
        }
        {
            var Q0;
            Q0=makeQuery(id+"F21.opExtrude","SWEPT_BODY",BODY,{"disambiguationData":[OSD([sQuery(id+"F20.wireOp",EDGE,"E5.bottom"),sQuery(id+"F20.wireOp",EDGE,"E5.top"),sQuery(id+"F20.wireOp",EDGE,"E5.left"),sQuery(id+"F20.wireOp",EDGE,"E5.right")])]});
            var Q1;
            Q1=makeQuery(id+"F23.opPattern","COPY",BODY,{"derivedFrom":makeQuery(id+"F21.opExtrude","SWEPT_BODY",BODY,{"disambiguationData":[OSD([sQuery(id+"F20.wireOp",EDGE,"E5.bottom"),sQuery(id+"F20.wireOp",EDGE,"E5.top"),sQuery(id+"F20.wireOp",EDGE,"E5.left"),sQuery(id+"F20.wireOp",EDGE,"E5.right")])]}),"instanceName":"1"});
            transform(context, id + "F65", {"entities" : qUnion([Q0, Q1]), "transformType" : TransformType.TRANSLATION_3D, "dx" : 0 * mm, "dy" : -127 * mm, "dz" : 0 * mm, "makeCopy" : false});
        }
        {
            var Q0;
            Q0=makeQuery(id+"F39.opExtrude","SWEPT_BODY",BODY,{"disambiguationData":[OSD([sQuery(id+"F38.wireOp",EDGE,"E9.bottom"),sQuery(id+"F38.wireOp",EDGE,"E9.top"),sQuery(id+"F38.wireOp",EDGE,"E9.left"),sQuery(id+"F38.wireOp",EDGE,"E9.right")])]});
            transform(context, id + "F66", {"entities" : qUnion([Q0]), "transformType" : TransformType.TRANSLATION_3D, "dx" : 0 * mm, "dy" : 0 * mm, "dz" : -127 * mm, "makeCopy" : false});
        }
        {
            var Q0;
            Q0=makeQuery(id+"F40.opPattern","COPY",BODY,{"derivedFrom":makeQuery(id+"F39.opExtrude","SWEPT_BODY",BODY,{"disambiguationData":[OSD([sQuery(id+"F38.wireOp",EDGE,"E9.bottom"),sQuery(id+"F38.wireOp",EDGE,"E9.top"),sQuery(id+"F38.wireOp",EDGE,"E9.left"),sQuery(id+"F38.wireOp",EDGE,"E9.right")])]}),"instanceName":"1"});
            transform(context, id + "F67", {"entities" : qUnion([Q0]), "transformType" : TransformType.TRANSLATION_3D, "dx" : 0 * mm, "dy" : 0 * mm, "dz" : -127 * mm, "makeCopy" : false});
        }
        {
            var Q0;
            Q0=makeQuery(id+"F16.opExtrude","SWEPT_BODY",BODY,{"disambiguationData":[OSD([sQuery(id+"F15.wireOp",EDGE,"E4.bottom"),sQuery(id+"F15.wireOp",EDGE,"E4.top"),sQuery(id+"F15.wireOp",EDGE,"E4.left"),sQuery(id+"F15.wireOp",EDGE,"E4.right")])]});
            transform(context, id + "F68", {"entities" : qUnion([Q0]), "transformType" : TransformType.TRANSLATION_3D, "dx" : 0 * mm, "dy" : 50.8 * mm, "dz" : 76.2 * mm, "makeCopy" : false});
        }
        {
            var Q0;
            Q0=makeQuery(id+"F17.opPattern","COPY",BODY,{"derivedFrom":makeQuery(id+"F16.opExtrude","SWEPT_BODY",BODY,{"disambiguationData":[OSD([sQuery(id+"F15.wireOp",EDGE,"E4.bottom"),sQuery(id+"F15.wireOp",EDGE,"E4.top"),sQuery(id+"F15.wireOp",EDGE,"E4.left"),sQuery(id+"F15.wireOp",EDGE,"E4.right")])]}),"instanceName":"1"});
            transform(context, id + "F69", {"entities" : qUnion([Q0]), "transformType" : TransformType.TRANSLATION_3D, "dx" : 0 * mm, "dy" : 50.8 * mm, "dz" : -76.2 * mm, "makeCopy" : false});
        }
    });
